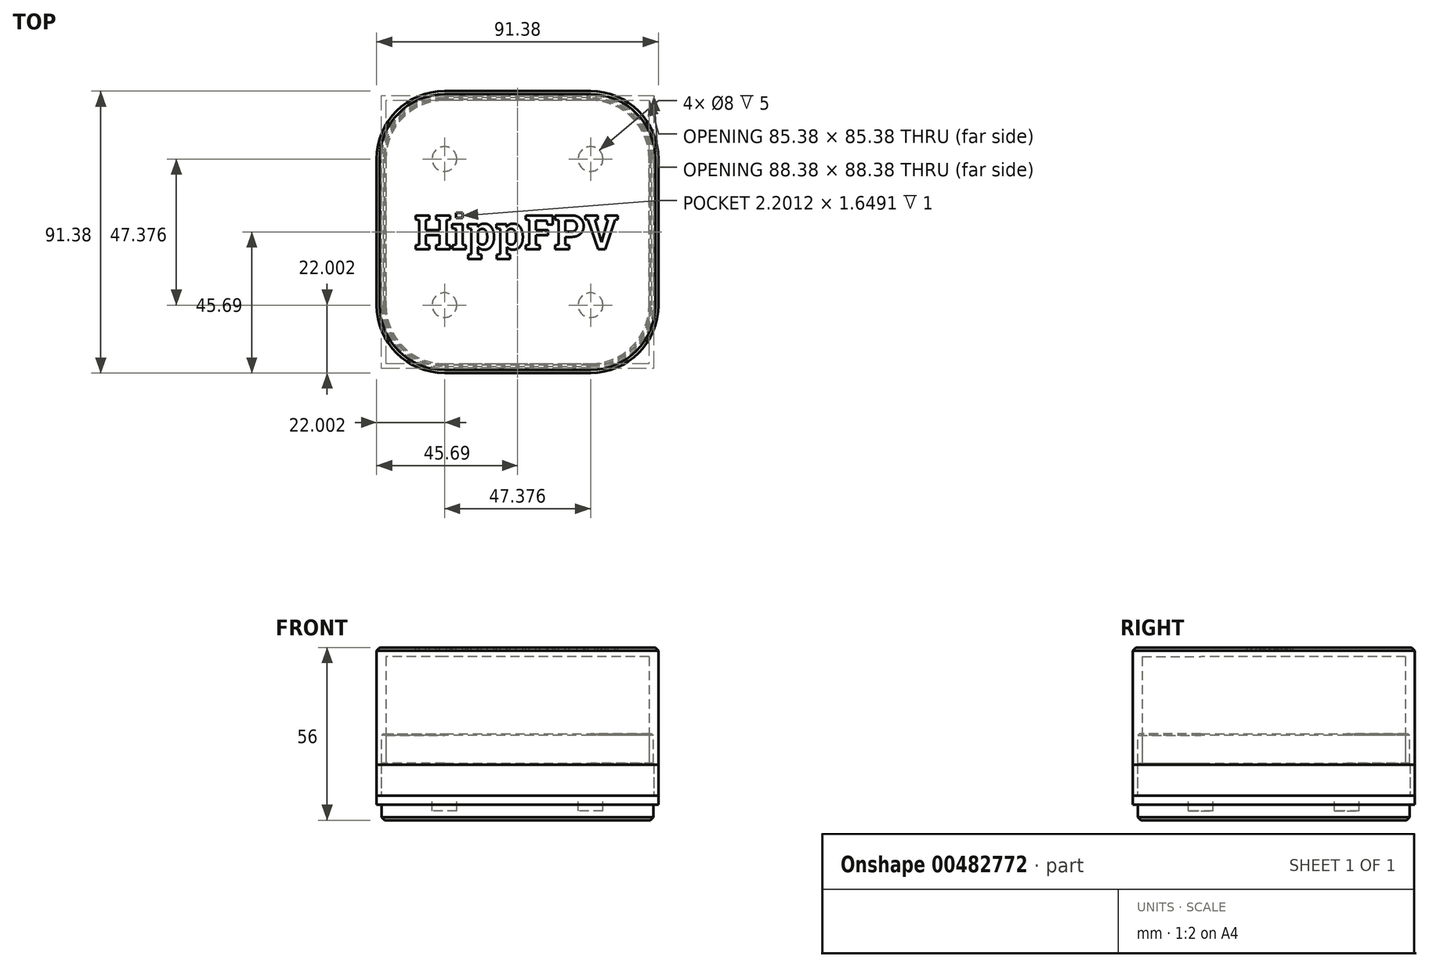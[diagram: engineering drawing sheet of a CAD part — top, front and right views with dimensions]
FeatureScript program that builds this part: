
annotation { "Feature Type Name" : "Feature", "Feature Type Description" : "" }
export const myFeature = defineFeature(function(context is Context, id is Id, definition is map)
    precondition{}
    {
        {
            var Q0;
            Q0=qCreatedBy(makeId("Top.planeOp"),FACE);
            var sketch = newSketch(context, id + "F0", { "sketchPlane" : qUnion([Q0])});
            skCircle(sketch, "E0", {"center": v(-23.69, 23.69) * mm, "radius": 18.5 * mm, "construction": true});
            skCircle(sketch, "E1", {"center": v(23.69, 23.69) * mm, "radius": 18.5 * mm, "construction": true});
            skCircle(sketch, "E2", {"center": v(-23.69, -23.69) * mm, "radius": 18.5 * mm, "construction": true});
            skCircle(sketch, "E3", {"center": v(23.69, -23.69) * mm, "radius": 18.5 * mm, "construction": true});
            skLineSegment(sketch, "E4.bottom", {"start": v(-23.69, 23.69) * mm, "end": v(23.69, 23.69) * mm, "construction": true});
            skLineSegment(sketch, "E4.top", {"start": v(-23.69, -23.69) * mm, "end": v(23.69, -23.69) * mm, "construction": true});
            skLineSegment(sketch, "E4.left", {"start": v(-23.69, 23.69) * mm, "end": v(-23.69, -23.69) * mm, "construction": true});
            skLineSegment(sketch, "E4.right", {"start": v(23.69, 23.69) * mm, "end": v(23.69, -23.69) * mm, "construction": true});
            skLineSegment(sketch, "E5", {"start": v(-23.69, 23.69) * mm, "end": v(23.69, -23.69) * mm, "construction": true});
            skLineSegment(sketch, "E6", {"start": v(-42.19, 23.69) * mm, "end": v(-42.19, -23.69) * mm, "construction": true});
            skLineSegment(sketch, "E7", {"start": v(-23.69, -42.19) * mm, "end": v(23.69, -42.19) * mm, "construction": true});
            skLineSegment(sketch, "E8", {"start": v(42.19, -23.69) * mm, "end": v(42.19, 23.69) * mm, "construction": true});
            skLineSegment(sketch, "E9", {"start": v(23.69, 42.19) * mm, "end": v(-23.69, 42.19) * mm, "construction": true});
            skSolve(sketch);
        }
        {
            var Q0;
            Q0=qCreatedBy(makeId("Top.planeOp"),FACE);
            var sketch = newSketch(context, id + "F1", { "sketchPlane" : qUnion([Q0])});
            skArc(sketch, "E10.0", {"start": v(42.19, 23.69) * mm, "mid": v(36.77, 36.77) * mm, "end": v(23.69, 42.19) * mm, "construction": true});
            skLineSegment(sketch, "E10.1", {"start": v(-23.69, -42.19) * mm, "end": v(23.69, -42.19) * mm, "construction": true});
            skArc(sketch, "E10.2", {"start": v(-23.69, 42.19) * mm, "mid": v(-36.77, 36.77) * mm, "end": v(-42.19, 23.69) * mm, "construction": true});
            skLineSegment(sketch, "E10.3", {"start": v(-42.19, 23.69) * mm, "end": v(-42.19, -23.69) * mm, "construction": true});
            skArc(sketch, "E10.4", {"start": v(23.69, -42.19) * mm, "mid": v(36.77, -36.77) * mm, "end": v(42.19, -23.69) * mm, "construction": true});
            skLineSegment(sketch, "E10.5", {"start": v(23.69, 42.19) * mm, "end": v(-23.69, 42.19) * mm, "construction": true});
            skArc(sketch, "E10.6", {"start": v(-42.19, -23.69) * mm, "mid": v(-36.77, -36.77) * mm, "end": v(-23.69, -42.19) * mm, "construction": true});
            skLineSegment(sketch, "E10.7", {"start": v(42.19, -23.69) * mm, "end": v(42.19, 23.69) * mm, "construction": true});
            skArc(sketch, "E11.0", {"start": v(-42.69, -23.69) * mm, "mid": v(-37.12, -37.12) * mm, "end": v(-23.69, -42.69) * mm});
            skLineSegment(sketch, "E11.1", {"start": v(-42.69, 23.69) * mm, "end": v(-42.69, -23.69) * mm});
            skLineSegment(sketch, "E11.2", {"start": v(-23.69, -42.69) * mm, "end": v(23.69, -42.69) * mm});
            skArc(sketch, "E11.3", {"start": v(-23.69, 42.69) * mm, "mid": v(-37.12, 37.12) * mm, "end": v(-42.69, 23.69) * mm});
            skArc(sketch, "E11.4", {"start": v(23.69, -42.69) * mm, "mid": v(37.12, -37.12) * mm, "end": v(42.69, -23.69) * mm});
            skLineSegment(sketch, "E11.5", {"start": v(42.69, -23.69) * mm, "end": v(42.69, 23.69) * mm});
            skArc(sketch, "E11.6", {"start": v(42.69, 23.69) * mm, "mid": v(37.12, 37.12) * mm, "end": v(23.69, 42.69) * mm});
            skLineSegment(sketch, "E11.7", {"start": v(23.69, 42.69) * mm, "end": v(-23.69, 42.69) * mm});
            skSolve(sketch);
        }
        {
            var Q0;
            Q0=qCreatedBy(makeId("Top.planeOp"),FACE);
            var sketch = newSketch(context, id + "F2", { "sketchPlane" : qUnion([Q0])});
            skLineSegment(sketch, "E12.0", {"start": v(23.69, 42.69) * mm, "end": v(-23.69, 42.69) * mm, "construction": true});
            skLineSegment(sketch, "E12.1", {"start": v(-23.69, -42.69) * mm, "end": v(23.69, -42.69) * mm, "construction": true});
            skArc(sketch, "E12.2", {"start": v(42.69, 23.69) * mm, "mid": v(37.12, 37.12) * mm, "end": v(23.69, 42.69) * mm, "construction": true});
            skLineSegment(sketch, "E12.3", {"start": v(-42.69, 23.69) * mm, "end": v(-42.69, -23.69) * mm, "construction": true});
            skLineSegment(sketch, "E12.4", {"start": v(42.69, -23.69) * mm, "end": v(42.69, 23.69) * mm, "construction": true});
            skArc(sketch, "E12.5", {"start": v(-42.69, -23.69) * mm, "mid": v(-37.12, -37.12) * mm, "end": v(-23.69, -42.69) * mm, "construction": true});
            skArc(sketch, "E12.6", {"start": v(23.69, -42.69) * mm, "mid": v(37.12, -37.12) * mm, "end": v(42.69, -23.69) * mm, "construction": true});
            skArc(sketch, "E12.7", {"start": v(-23.69, 42.69) * mm, "mid": v(-37.12, 37.12) * mm, "end": v(-42.69, 23.69) * mm, "construction": true});
            skArc(sketch, "E13.0", {"start": v(45.69, 23.69) * mm, "mid": v(39.24, 39.24) * mm, "end": v(23.69, 45.69) * mm});
            skLineSegment(sketch, "E13.1", {"start": v(45.69, -23.69) * mm, "end": v(45.69, 23.69) * mm});
            skLineSegment(sketch, "E13.2", {"start": v(23.69, 45.69) * mm, "end": v(-23.69, 45.69) * mm});
            skArc(sketch, "E13.3", {"start": v(23.69, -45.69) * mm, "mid": v(39.24, -39.24) * mm, "end": v(45.69, -23.69) * mm});
            skArc(sketch, "E13.4", {"start": v(-23.69, 45.69) * mm, "mid": v(-39.24, 39.24) * mm, "end": v(-45.69, 23.69) * mm});
            skLineSegment(sketch, "E13.5", {"start": v(-45.69, 23.69) * mm, "end": v(-45.69, -23.69) * mm});
            skArc(sketch, "E13.6", {"start": v(-45.69, -23.69) * mm, "mid": v(-39.24, -39.24) * mm, "end": v(-23.69, -45.69) * mm});
            skLineSegment(sketch, "E13.7", {"start": v(-23.69, -45.69) * mm, "end": v(23.69, -45.69) * mm});
            skSolve(sketch);
        }
        {
            var Q0;
            Q0 = qSketchRegion(id + "F2", true);
            extrude(context, id + "F3", {"entities" : qUnion([Q0]), "oppositeDirection" : true, "depth" : 8 * mm, "offsetDistance" : 25 * mm});
        }
        {
            var Q0;
            Q0=makeQuery(id+"F3.opExtrude","CAP_FACE",FACE,{"disambiguationData":[OSD([sQuery(id+"F2.wireOp",EDGE,"E13.0"),sQuery(id+"F2.wireOp",EDGE,"E13.1"),sQuery(id+"F2.wireOp",EDGE,"E13.2"),sQuery(id+"F2.wireOp",EDGE,"E13.3"),sQuery(id+"F2.wireOp",EDGE,"E13.4"),sQuery(id+"F2.wireOp",EDGE,"E13.5"),sQuery(id+"F2.wireOp",EDGE,"E13.6"),sQuery(id+"F2.wireOp",EDGE,"E13.7")])],"isStart":true});
            var sketch = newSketch(context, id + "F4", { "sketchPlane" : qUnion([Q0])});
            skArc(sketch, "E14.0", {"start": v(42.19, 23.69) * mm, "mid": v(36.77, 36.77) * mm, "end": v(23.69, 42.19) * mm, "construction": true});
            skLineSegment(sketch, "E14.1", {"start": v(-23.69, -42.19) * mm, "end": v(23.69, -42.19) * mm, "construction": true});
            skArc(sketch, "E14.2", {"start": v(-23.69, 42.19) * mm, "mid": v(-36.77, 36.77) * mm, "end": v(-42.19, 23.69) * mm, "construction": true});
            skLineSegment(sketch, "E14.3", {"start": v(-42.19, 23.69) * mm, "end": v(-42.19, -23.69) * mm, "construction": true});
            skArc(sketch, "E14.4", {"start": v(23.69, -42.19) * mm, "mid": v(36.77, -36.77) * mm, "end": v(42.19, -23.69) * mm, "construction": true});
            skLineSegment(sketch, "E14.5", {"start": v(23.69, 42.19) * mm, "end": v(-23.69, 42.19) * mm, "construction": true});
            skArc(sketch, "E14.6", {"start": v(-42.19, -23.69) * mm, "mid": v(-36.77, -36.77) * mm, "end": v(-23.69, -42.19) * mm, "construction": true});
            skLineSegment(sketch, "E14.7", {"start": v(42.19, -23.69) * mm, "end": v(42.19, 23.69) * mm, "construction": true});
            skArc(sketch, "E15.0", {"start": v(-23.69, 45.69) * mm, "mid": v(-39.24, 39.24) * mm, "end": v(-45.69, 23.69) * mm});
            skLineSegment(sketch, "E15.1", {"start": v(23.69, 45.69) * mm, "end": v(-23.69, 45.69) * mm});
            skLineSegment(sketch, "E15.2", {"start": v(-45.69, 23.69) * mm, "end": v(-45.69, -23.69) * mm});
            skArc(sketch, "E15.3", {"start": v(45.69, 23.69) * mm, "mid": v(39.24, 39.24) * mm, "end": v(23.69, 45.69) * mm});
            skArc(sketch, "E15.4", {"start": v(-45.69, -23.69) * mm, "mid": v(-39.24, -39.24) * mm, "end": v(-23.69, -45.69) * mm});
            skLineSegment(sketch, "E15.5", {"start": v(-23.69, -45.69) * mm, "end": v(23.69, -45.69) * mm});
            skArc(sketch, "E15.6", {"start": v(23.69, -45.69) * mm, "mid": v(39.24, -39.24) * mm, "end": v(45.69, -23.69) * mm});
            skLineSegment(sketch, "E15.7", {"start": v(45.69, -23.69) * mm, "end": v(45.69, 23.69) * mm});
            skArc(sketch, "E16.0", {"start": v(-42.69, -23.69) * mm, "mid": v(-37.12, -37.12) * mm, "end": v(-23.69, -42.69) * mm});
            skLineSegment(sketch, "E16.1", {"start": v(-42.69, 23.69) * mm, "end": v(-42.69, -23.69) * mm});
            skLineSegment(sketch, "E16.2", {"start": v(-23.69, -42.69) * mm, "end": v(23.69, -42.69) * mm});
            skArc(sketch, "E16.3", {"start": v(-23.69, 42.69) * mm, "mid": v(-37.12, 37.12) * mm, "end": v(-42.69, 23.69) * mm});
            skArc(sketch, "E16.4", {"start": v(23.69, -42.69) * mm, "mid": v(37.12, -37.12) * mm, "end": v(42.69, -23.69) * mm});
            skLineSegment(sketch, "E16.5", {"start": v(42.69, -23.69) * mm, "end": v(42.69, 23.69) * mm});
            skArc(sketch, "E16.6", {"start": v(42.69, 23.69) * mm, "mid": v(37.12, 37.12) * mm, "end": v(23.69, 42.69) * mm});
            skLineSegment(sketch, "E16.7", {"start": v(23.69, 42.69) * mm, "end": v(-23.69, 42.69) * mm});
            skSolve(sketch);
        }
        {
            var Q0;
            Q0 = qSketchRegion(id + "F4", true);
            extrude(context, id + "F5", {"entities" : qUnion([Q0]), "operationType" : NewBodyOperationType.ADD, "depth" : 20 * mm, "offsetDistance" : 25 * mm});
        }
        {
            var Q0;
            Q0=makeQuery(id+"F3.opExtrude","CAP_FACE",FACE,{"disambiguationData":[OSD([sQuery(id+"F2.wireOp",EDGE,"E13.0"),sQuery(id+"F2.wireOp",EDGE,"E13.1"),sQuery(id+"F2.wireOp",EDGE,"E13.2"),sQuery(id+"F2.wireOp",EDGE,"E13.3"),sQuery(id+"F2.wireOp",EDGE,"E13.4"),sQuery(id+"F2.wireOp",EDGE,"E13.5"),sQuery(id+"F2.wireOp",EDGE,"E13.6"),sQuery(id+"F2.wireOp",EDGE,"E13.7")])],"isStart":true});
            var sketch = newSketch(context, id + "F6", { "sketchPlane" : qUnion([Q0])});
            skCircle(sketch, "E17", {"center": v(-23.69, 23.69) * mm, "radius": 4 * mm});
            skCircle(sketch, "E18", {"center": v(23.69, 23.69) * mm, "radius": 4 * mm});
            skCircle(sketch, "E19", {"center": v(23.69, -23.69) * mm, "radius": 4 * mm});
            skCircle(sketch, "E20", {"center": v(-23.69, -23.69) * mm, "radius": 4 * mm});
            skSolve(sketch);
        }
        {
            var Q0;
            Q0 = qSketchRegion(id + "F6", true);
            extrude(context, id + "F7", {"entities" : qUnion([Q0]), "operationType" : NewBodyOperationType.REMOVE, "oppositeDirection" : true, "depth" : 5 * mm, "offsetDistance" : 25 * mm});
        }
        {
            var Q0;
            Q0=makeQuery(id+"F5.opExtrude","CAP_FACE",FACE,{"disambiguationData":[OSD([sQuery(id+"F4.wireOp",EDGE,"E15.0"),sQuery(id+"F4.wireOp",EDGE,"E15.1"),sQuery(id+"F4.wireOp",EDGE,"E15.2"),sQuery(id+"F4.wireOp",EDGE,"E15.3"),sQuery(id+"F4.wireOp",EDGE,"E15.4"),sQuery(id+"F4.wireOp",EDGE,"E15.5"),sQuery(id+"F4.wireOp",EDGE,"E15.6"),sQuery(id+"F4.wireOp",EDGE,"E15.7"),sQuery(id+"F4.wireOp",EDGE,"E16.0"),sQuery(id+"F4.wireOp",EDGE,"E16.1"),sQuery(id+"F4.wireOp",EDGE,"E16.2"),sQuery(id+"F4.wireOp",EDGE,"E16.3"),sQuery(id+"F4.wireOp",EDGE,"E16.4"),sQuery(id+"F4.wireOp",EDGE,"E16.5"),sQuery(id+"F4.wireOp",EDGE,"E16.6"),sQuery(id+"F4.wireOp",EDGE,"E16.7")])],"isStart":false});
            var sketch = newSketch(context, id + "F8", { "sketchPlane" : qUnion([Q0])});
            skLineSegment(sketch, "E21.0", {"start": v(-44.09, 23.69) * mm, "end": v(-44.09, -23.69) * mm});
            skArc(sketch, "E21.1", {"start": v(-23.69, 44.09) * mm, "mid": v(-38.11, 38.11) * mm, "end": v(-44.09, 23.69) * mm});
            skArc(sketch, "E21.2", {"start": v(-44.09, -23.69) * mm, "mid": v(-38.11, -38.11) * mm, "end": v(-23.69, -44.09) * mm});
            skLineSegment(sketch, "E21.3", {"start": v(23.69, 44.09) * mm, "end": v(-23.69, 44.09) * mm});
            skLineSegment(sketch, "E21.4", {"start": v(-23.69, -44.09) * mm, "end": v(23.69, -44.09) * mm});
            skArc(sketch, "E21.5", {"start": v(23.69, -44.09) * mm, "mid": v(38.11, -38.11) * mm, "end": v(44.09, -23.69) * mm});
            skLineSegment(sketch, "E21.6", {"start": v(44.09, -23.69) * mm, "end": v(44.09, 23.69) * mm});
            skArc(sketch, "E21.7", {"start": v(44.09, 23.69) * mm, "mid": v(38.11, 38.11) * mm, "end": v(23.69, 44.09) * mm});
            skArc(sketch, "E22.0", {"start": v(-45.69, -23.69) * mm, "mid": v(-39.24, -39.24) * mm, "end": v(-23.69, -45.69) * mm});
            skArc(sketch, "E22.1", {"start": v(-23.69, 45.69) * mm, "mid": v(-39.24, 39.24) * mm, "end": v(-45.69, 23.69) * mm});
            skLineSegment(sketch, "E22.2", {"start": v(45.69, -23.69) * mm, "end": v(45.69, 23.69) * mm});
            skLineSegment(sketch, "E22.3", {"start": v(-45.69, 23.69) * mm, "end": v(-45.69, -23.69) * mm});
            skArc(sketch, "E22.4", {"start": v(45.69, 23.69) * mm, "mid": v(39.24, 39.24) * mm, "end": v(23.69, 45.69) * mm});
            skArc(sketch, "E22.5", {"start": v(23.69, -45.69) * mm, "mid": v(39.24, -39.24) * mm, "end": v(45.69, -23.69) * mm});
            skLineSegment(sketch, "E22.6", {"start": v(-23.69, -45.69) * mm, "end": v(23.69, -45.69) * mm});
            skLineSegment(sketch, "E22.7", {"start": v(23.69, 45.69) * mm, "end": v(-23.69, 45.69) * mm});
            skSolve(sketch);
        }
        {
            var Q0;
            Q0 = qSketchRegion(id + "F8", true);
            extrude(context, id + "F9", {"entities" : qUnion([Q0]), "operationType" : NewBodyOperationType.REMOVE, "oppositeDirection" : true, "depth" : 10 * mm, "offsetDistance" : 25 * mm});
        }
        {
            var Q0;
            Q0=makeQuery(id+"F3.opExtrude","CAP_FACE",FACE,{"disambiguationData":[OSD([sQuery(id+"F2.wireOp",EDGE,"E13.0"),sQuery(id+"F2.wireOp",EDGE,"E13.1"),sQuery(id+"F2.wireOp",EDGE,"E13.2"),sQuery(id+"F2.wireOp",EDGE,"E13.3"),sQuery(id+"F2.wireOp",EDGE,"E13.4"),sQuery(id+"F2.wireOp",EDGE,"E13.5"),sQuery(id+"F2.wireOp",EDGE,"E13.6"),sQuery(id+"F2.wireOp",EDGE,"E13.7")])],"isStart":false});
            var sketch = newSketch(context, id + "F10", { "sketchPlane" : qUnion([Q0])});
            skArc(sketch, "E23.0", {"start": v(45.69, -23.69) * mm, "mid": v(39.24, -39.24) * mm, "end": v(23.69, -45.69) * mm});
            skLineSegment(sketch, "E23.1", {"start": v(23.69, -45.69) * mm, "end": v(-23.69, -45.69) * mm});
            skLineSegment(sketch, "E23.2", {"start": v(-23.69, 45.69) * mm, "end": v(23.69, 45.69) * mm});
            skArc(sketch, "E23.3", {"start": v(-45.69, 23.69) * mm, "mid": v(-39.24, 39.24) * mm, "end": v(-23.69, 45.69) * mm});
            skLineSegment(sketch, "E23.4", {"start": v(45.69, 23.69) * mm, "end": v(45.69, -23.69) * mm});
            skLineSegment(sketch, "E23.5", {"start": v(-45.69, -23.69) * mm, "end": v(-45.69, 23.69) * mm});
            skArc(sketch, "E23.6", {"start": v(23.69, 45.69) * mm, "mid": v(39.24, 39.24) * mm, "end": v(45.69, 23.69) * mm});
            skArc(sketch, "E23.7", {"start": v(-23.69, -45.69) * mm, "mid": v(-39.24, -39.24) * mm, "end": v(-45.69, -23.69) * mm});
            skLineSegment(sketch, "E24.0", {"start": v(-44.09, -23.69) * mm, "end": v(-44.09, 23.69) * mm});
            skArc(sketch, "E24.1", {"start": v(-23.69, -44.09) * mm, "mid": v(-38.11, -38.11) * mm, "end": v(-44.09, -23.69) * mm});
            skArc(sketch, "E24.2", {"start": v(-44.09, 23.69) * mm, "mid": v(-38.11, 38.11) * mm, "end": v(-23.69, 44.09) * mm});
            skLineSegment(sketch, "E24.3", {"start": v(23.69, -44.09) * mm, "end": v(-23.69, -44.09) * mm});
            skLineSegment(sketch, "E24.4", {"start": v(-23.69, 44.09) * mm, "end": v(23.69, 44.09) * mm});
            skArc(sketch, "E24.5", {"start": v(23.69, 44.09) * mm, "mid": v(38.11, 38.11) * mm, "end": v(44.09, 23.69) * mm});
            skLineSegment(sketch, "E24.6", {"start": v(44.09, 23.69) * mm, "end": v(44.09, -23.69) * mm});
            skArc(sketch, "E24.7", {"start": v(44.09, -23.69) * mm, "mid": v(38.11, -38.11) * mm, "end": v(23.69, -44.09) * mm});
            skSolve(sketch);
        }
        {
            var Q0;
            Q0 = qSketchRegion(id + "F10", true);
            extrude(context, id + "F11", {"entities" : qUnion([Q0]), "operationType" : NewBodyOperationType.REMOVE, "oppositeDirection" : true, "depth" : 5 * mm, "offsetDistance" : 25 * mm});
        }
        {
            var Q0;
            Q0=makeQuery(id+"F3.opExtrude","CAP_FACE",FACE,{"disambiguationData":[OSD([sQuery(id+"F2.wireOp",EDGE,"E13.0"),sQuery(id+"F2.wireOp",EDGE,"E13.1"),sQuery(id+"F2.wireOp",EDGE,"E13.2"),sQuery(id+"F2.wireOp",EDGE,"E13.3"),sQuery(id+"F2.wireOp",EDGE,"E13.4"),sQuery(id+"F2.wireOp",EDGE,"E13.5"),sQuery(id+"F2.wireOp",EDGE,"E13.6"),sQuery(id+"F2.wireOp",EDGE,"E13.7")])],"isStart":false});
            chamfer(context, id + "F12", {"entities" : qUnion([Q0]), "width" : 1 * mm, "tangentPropagation" : true});
        }
        {
            var Q0;
            Q0=makeQuery(id+"F5.opExtrude","CAP_FACE",FACE,{"disambiguationData":[OSD([sQuery(id+"F4.wireOp",EDGE,"E15.0"),sQuery(id+"F4.wireOp",EDGE,"E15.1"),sQuery(id+"F4.wireOp",EDGE,"E15.2"),sQuery(id+"F4.wireOp",EDGE,"E15.3"),sQuery(id+"F4.wireOp",EDGE,"E15.4"),sQuery(id+"F4.wireOp",EDGE,"E15.5"),sQuery(id+"F4.wireOp",EDGE,"E15.6"),sQuery(id+"F4.wireOp",EDGE,"E15.7"),sQuery(id+"F4.wireOp",EDGE,"E16.0"),sQuery(id+"F4.wireOp",EDGE,"E16.1"),sQuery(id+"F4.wireOp",EDGE,"E16.2"),sQuery(id+"F4.wireOp",EDGE,"E16.3"),sQuery(id+"F4.wireOp",EDGE,"E16.4"),sQuery(id+"F4.wireOp",EDGE,"E16.5"),sQuery(id+"F4.wireOp",EDGE,"E16.6"),sQuery(id+"F4.wireOp",EDGE,"E16.7")])],"isStart":false});
            chamfer(context, id + "F13", {"entities" : qUnion([Q0]), "width" : .5 * mm, "tangentPropagation" : true});
        }
        {
            var Q0;
            Q0 = qSketchRegion(id + "F2", true);
            extrude(context, id + "F14", {"entities" : qUnion([Q0]), "depth" : 48 * mm, "offsetDistance" : 25 * mm});
        }
        {
            var Q0;
            Q0 = qSketchRegion(id + "F1", true);
            extrude(context, id + "F15", {"entities" : qUnion([Q0]), "operationType" : NewBodyOperationType.REMOVE, "depth" : 45 * mm, "offsetDistance" : 25 * mm});
        }
        {
            var Q0;
            Q0=makeQuery(id+"F14.opExtrude","CAP_FACE",FACE,{"disambiguationData":[OSD([sQuery(id+"F2.wireOp",EDGE,"E13.0"),sQuery(id+"F2.wireOp",EDGE,"E13.1"),sQuery(id+"F2.wireOp",EDGE,"E13.2"),sQuery(id+"F2.wireOp",EDGE,"E13.3"),sQuery(id+"F2.wireOp",EDGE,"E13.4"),sQuery(id+"F2.wireOp",EDGE,"E13.5"),sQuery(id+"F2.wireOp",EDGE,"E13.6"),sQuery(id+"F2.wireOp",EDGE,"E13.7")])],"isStart":true});
            var sketch = newSketch(context, id + "F16", { "sketchPlane" : qUnion([Q0])});
            skArc(sketch, "E25.0", {"start": v(-42.69, 23.69) * mm, "mid": v(-37.12, 37.12) * mm, "end": v(-23.69, 42.69) * mm});
            skLineSegment(sketch, "E25.1", {"start": v(-23.69, 42.69) * mm, "end": v(23.69, 42.69) * mm});
            skArc(sketch, "E25.2", {"start": v(42.69, -23.69) * mm, "mid": v(37.12, -37.12) * mm, "end": v(23.69, -42.69) * mm});
            skLineSegment(sketch, "E25.3", {"start": v(-42.69, -23.69) * mm, "end": v(-42.69, 23.69) * mm});
            skLineSegment(sketch, "E25.4", {"start": v(42.69, 23.69) * mm, "end": v(42.69, -23.69) * mm});
            skArc(sketch, "E25.5", {"start": v(-23.69, -42.69) * mm, "mid": v(-37.12, -37.12) * mm, "end": v(-42.69, -23.69) * mm});
            skLineSegment(sketch, "E25.6", {"start": v(23.69, -42.69) * mm, "end": v(-23.69, -42.69) * mm});
            skArc(sketch, "E25.7", {"start": v(23.69, 42.69) * mm, "mid": v(37.12, 37.12) * mm, "end": v(42.69, 23.69) * mm});
            skLineSegment(sketch, "E26.0", {"start": v(-23.69, 44.19) * mm, "end": v(23.69, 44.19) * mm});
            skArc(sketch, "E26.1", {"start": v(-44.19, 23.69) * mm, "mid": v(-38.18, 38.18) * mm, "end": v(-23.69, 44.19) * mm});
            skArc(sketch, "E26.2", {"start": v(23.69, 44.19) * mm, "mid": v(38.18, 38.18) * mm, "end": v(44.19, 23.69) * mm});
            skLineSegment(sketch, "E26.3", {"start": v(-44.19, -23.69) * mm, "end": v(-44.19, 23.69) * mm});
            skLineSegment(sketch, "E26.4", {"start": v(44.19, 23.69) * mm, "end": v(44.19, -23.69) * mm});
            skArc(sketch, "E26.5", {"start": v(44.19, -23.69) * mm, "mid": v(38.18, -38.18) * mm, "end": v(23.69, -44.19) * mm});
            skLineSegment(sketch, "E26.6", {"start": v(23.69, -44.19) * mm, "end": v(-23.69, -44.19) * mm});
            skArc(sketch, "E26.7", {"start": v(-23.69, -44.19) * mm, "mid": v(-38.18, -38.18) * mm, "end": v(-44.19, -23.69) * mm});
            skSolve(sketch);
        }
        {
            var Q0;
            Q0 = qSketchRegion(id + "F16", true);
            extrude(context, id + "F17", {"entities" : qUnion([Q0]), "operationType" : NewBodyOperationType.REMOVE, "oppositeDirection" : true, "depth" : 10.5 * mm, "offsetDistance" : 25 * mm});
        }
        {
            var Q0;
            Q0=makeQuery(id+"F14.opExtrude","CAP_FACE",FACE,{"disambiguationData":[OSD([sQuery(id+"F2.wireOp",EDGE,"E13.0"),sQuery(id+"F2.wireOp",EDGE,"E13.1"),sQuery(id+"F2.wireOp",EDGE,"E13.2"),sQuery(id+"F2.wireOp",EDGE,"E13.3"),sQuery(id+"F2.wireOp",EDGE,"E13.4"),sQuery(id+"F2.wireOp",EDGE,"E13.5"),sQuery(id+"F2.wireOp",EDGE,"E13.6"),sQuery(id+"F2.wireOp",EDGE,"E13.7")])],"isStart":false});
            chamfer(context, id + "F18", {"entities" : qUnion([Q0]), "width" : 1 * mm, "tangentPropagation" : true});
        }
        {
            var Q0;
            Q0=makeQuery(id+"F14.opExtrude","CAP_FACE",FACE,{"disambiguationData":[OSD([sQuery(id+"F2.wireOp",EDGE,"E13.0"),sQuery(id+"F2.wireOp",EDGE,"E13.1"),sQuery(id+"F2.wireOp",EDGE,"E13.2"),sQuery(id+"F2.wireOp",EDGE,"E13.3"),sQuery(id+"F2.wireOp",EDGE,"E13.4"),sQuery(id+"F2.wireOp",EDGE,"E13.5"),sQuery(id+"F2.wireOp",EDGE,"E13.6"),sQuery(id+"F2.wireOp",EDGE,"E13.7")])],"isStart":false});
            var sketch = newSketch(context, id + "F19", { "sketchPlane" : qUnion([Q0])});
            skText(sketch, "E27", { "text": "HippFPV", "fontName": "RobotoSlab-Bold.ttf"});
            const initialGuessF19  = {"E27": [-0.0335, -0.00556, 1, 0, 0.01111]};
            skSetInitialGuess(sketch, initialGuessF19);
            skSolve(sketch);
        }
        {
            var Q0;
            Q0 = qSketchRegion(id + "F19", true);
            extrude(context, id + "F20", {"entities" : qUnion([Q0]), "operationType" : NewBodyOperationType.REMOVE, "oppositeDirection" : true, "depth" : 1 * mm, "offsetDistance" : 25 * mm});
        }
    });
